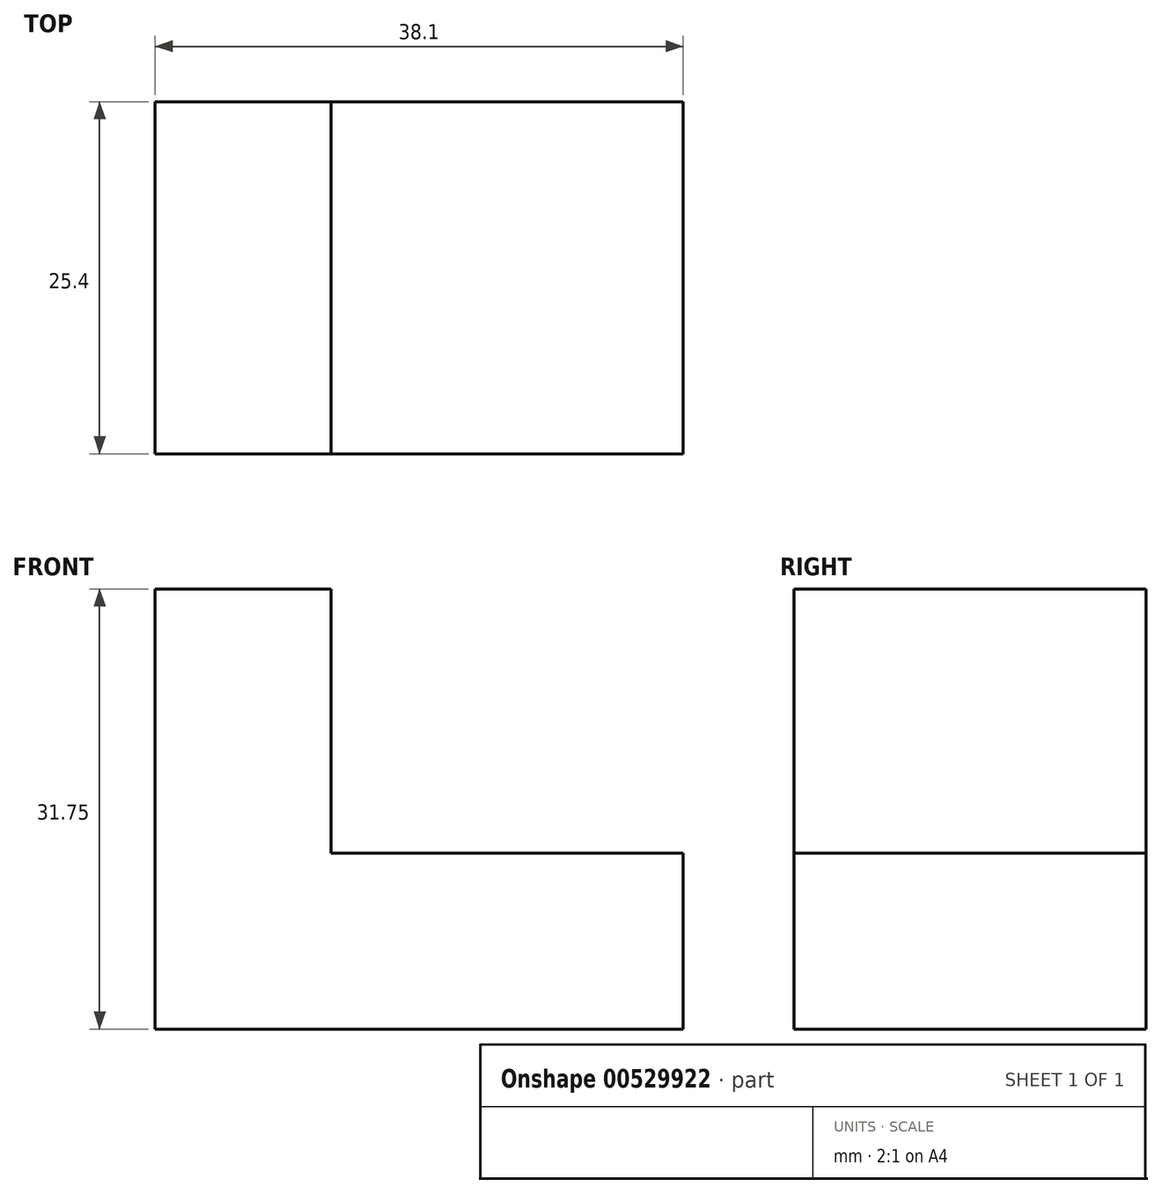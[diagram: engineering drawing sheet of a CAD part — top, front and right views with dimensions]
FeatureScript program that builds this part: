
annotation { "Feature Type Name" : "Feature", "Feature Type Description" : "" }
export const myFeature = defineFeature(function(context is Context, id is Id, definition is map)
    precondition{}
    {
        {
            var Q0;
            Q0=qCreatedBy(makeId("Front.planeOp"),FACE);
            var sketch = newSketch(context, id + "F0", { "sketchPlane" : qUnion([Q0])});
            skLineSegment(sketch, "E0", {"start": v(-56.74, 48.66) * mm, "end": v(-56.74, 16.9) * mm});
            skLineSegment(sketch, "E1", {"start": v(-56.74, 16.9) * mm, "end": v(-18.64, 16.9) * mm});
            skLineSegment(sketch, "E2", {"start": v(-18.64, 16.9) * mm, "end": v(-18.64, 29.6) * mm});
            skLineSegment(sketch, "E3", {"start": v(-18.64, 29.6) * mm, "end": v(-44.04, 29.6) * mm});
            skLineSegment(sketch, "E4", {"start": v(-44.04, 29.6) * mm, "end": v(-44.04, 48.66) * mm});
            skLineSegment(sketch, "E5", {"start": v(-44.04, 48.66) * mm, "end": v(-56.74, 48.66) * mm});
            skSolve(sketch);
        }
        {
            var Q0;
            Q0 = qSketchRegion(id + "F0", true);
            extrude(context, id + "F1", {"entities" : qUnion([Q0]), "depth" : 25.4 * mm, "offsetDistance" : 25.4 * mm});
        }
    });
